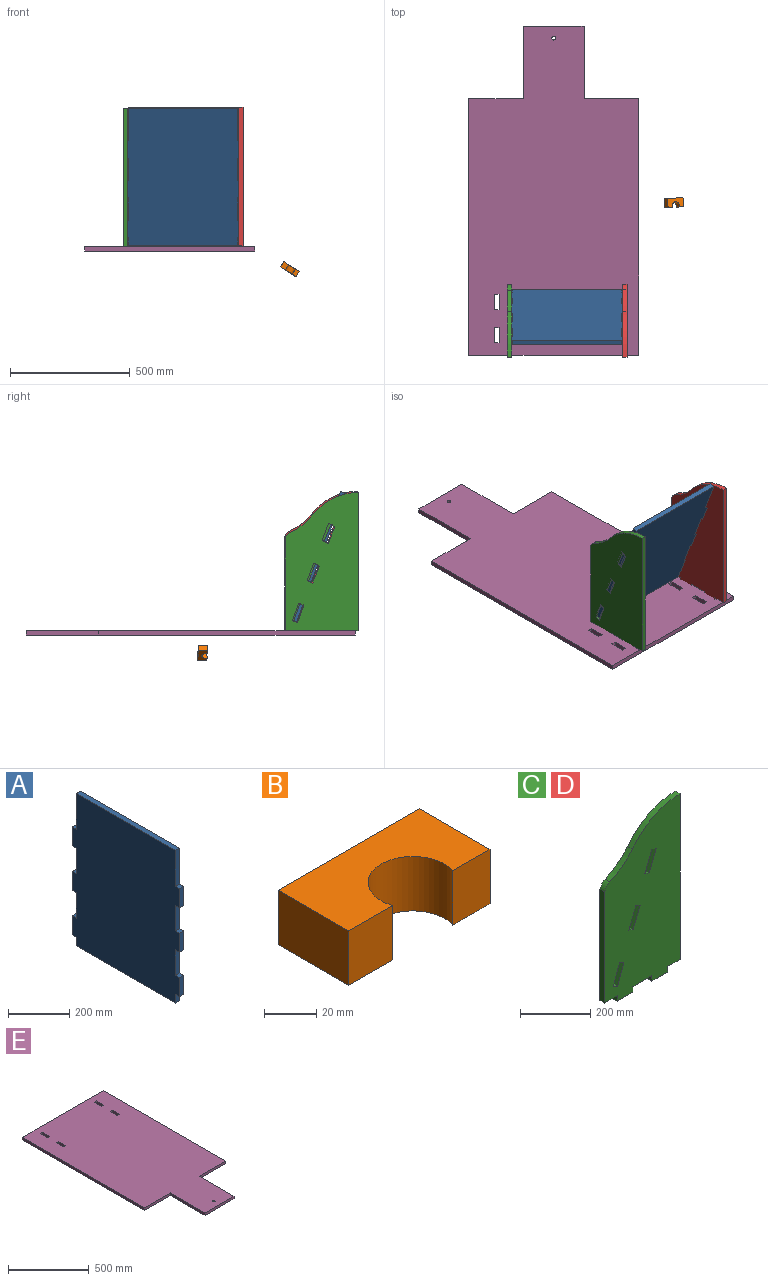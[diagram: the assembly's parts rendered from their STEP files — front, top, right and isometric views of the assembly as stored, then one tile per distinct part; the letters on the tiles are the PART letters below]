
ASSEMBLY  parts=5 mates=1
PART A: 30 faces, bbox 19.1x495.3x609.6 mm
  f0: plane 19.05x19.05mm, normal (0,0,-1), area 362.9mm2, adj f1,f27,f28,f29
  f1: plane 34.46x19.05mm, normal (0,-1,0), area 656.5mm2, adj f0,f2,f28,f29
  f2: plane 457.2x19.05mm, normal (0,0,-1), area 8709.7mm2, adj f1,f3,f28,f29
  f3: plane 34.46x19.05mm, normal (0,1,0), area 656.5mm2, adj f2,f4,f28,f29
  f4: plane 19.05x19.05mm, normal (0,0,-1), area 362.9mm2, adj f3,f5,f28,f29
  f5: plane 76.2x19.05mm, normal (0,1,0), area 1451.6mm2, adj f4,f6,f28,f29
  f6: plane 19.05x19.05mm, normal (0,0,1), area 362.9mm2, adj f5,f7,f28,f29
  f7: plane 101.6x19.05mm, normal (0,1,0), area 1935.5mm2, adj f6,f8,f28,f29
  f8: plane 19.05x19.05mm, normal (0,0,-1), area 362.9mm2, adj f7,f9,f28,f29
  f9: plane 76.2x19.05mm, normal (0,1,0), area 1451.6mm2, adj f8,f10,f28,f29
  f10: plane 19.05x19.05mm, normal (0,0,1), area 362.9mm2, adj f9,f11,f28,f29
  f11: plane 101.6x19.05mm, normal (0,1,0), area 1935.5mm2, adj f10,f12,f28,f29
  f12: plane 19.05x19.05mm, normal (0,0,-1), area 362.9mm2, adj f11,f13,f28,f29
  f13: plane 76.2x19.05mm, normal (0,1,0), area 1451.6mm2, adj f12,f14,f28,f29
  f14: plane 19.05x19.05mm, normal (0,0,1), area 362.9mm2, adj f13,f15,f28,f29
  f15: plane 143.34x19.05mm, normal (0,1,0), area 2730.6mm2, adj f14,f16,f28,f29
  f16: plane 457.2x19.05mm, normal (0,0,1), area 8709.7mm2, adj f15,f17,f28,f29
  f17: plane 143.34x19.05mm, normal (0,-1,0), area 2730.6mm2, adj f16,f18,f28,f29
  f18: plane 19.05x19.05mm, normal (0,0,1), area 362.9mm2, adj f17,f19,f28,f29
  f19: plane 76.2x19.05mm, normal (0,-1,0), area 1451.6mm2, adj f18,f20,f28,f29
  f20: plane 19.05x19.05mm, normal (0,0,-1), area 362.9mm2, adj f19,f21,f28,f29
  f21: plane 101.6x19.05mm, normal (0,-1,0), area 1935.5mm2, adj f20,f22,f28,f29
  f22: plane 19.05x19.05mm, normal (0,0,1), area 362.9mm2, adj f21,f23,f28,f29
  f23: plane 76.2x19.05mm, normal (0,-1,0), area 1451.6mm2, adj f22,f24,f28,f29
  f24: plane 19.05x19.05mm, normal (0,0,-1), area 362.9mm2, adj f23,f25,f28,f29
  f25: plane 101.6x19.05mm, normal (0,-1,0), area 1935.5mm2, adj f24,f26,f28,f29
  f26: plane 19.05x19.05mm, normal (0,0,1), area 362.9mm2, adj f25,f27,f28,f29
  f27: plane 76.2x19.05mm, normal (0,-1,0), area 1451.6mm2, adj f0,f26,f28,f29
  f28: plane 609.6x495.3mm, normal (1,0,0), area 287418.8mm2, adj f0,f1,f2,f3,f4,f5,f6,f7
  f29: plane 609.6x495.3mm, normal (-1,0,0), area 287418.8mm2, adj f0,f1,f2,f3,f4,f5,f6,f7
PART B: 8 faces, bbox 76.2x38.1x25.4 mm
  f0: plane 25.4x23.76mm, normal (0,-1,0), area 603.6mm2, adj f1,f2,f3,f7
  f1: plane 76.2x38.1mm, normal (0,0,1), area 2262.4mm2, adj f0,f3,f4,f5,f6,f7
  f2: plane 76.2x38.1mm, normal (0,0,-1), area 2262.4mm2, adj f0,f3,f4,f5,f6,f7
  f3: plane 38.1x25.4mm, normal (-1,0,0), area 967.7mm2, adj f0,f1,f2,f6
  f4: plane 25.4x19.95mm, normal (0,-1,0), area 506.8mm2, adj f1,f2,f5,f7
  f5: plane 38.1x25.4mm, normal (1,0,0), area 967.7mm2, adj f1,f2,f4,f6
  f6: plane 76.2x25.4mm, normal (0,1,0), area 1935.5mm2, adj f1,f2,f3,f5
  f7: cylinder r=17.11mm len=34.22mm, axis (0,0,-1), area 1643.2mm2, adj f0,f1,f2,f4
PART C: 28 faces, bbox 304.8x19.1x596.5 mm
  f0: plane 70.92x27.87mm, normal (0.93,0,-0.37), area 1451.6mm2, adj f1,f25,f26,f27
  f1: plane 19.05x17.73mm, normal (-0.37,0,-0.93), area 362.9mm2, adj f0,f2,f26,f27
  f2: plane 70.92x27.87mm, normal (-0.93,0,0.37), area 1451.6mm2, adj f1,f25,f26,f27
  f3: plane 577.48x19.05mm, normal (1,0,0), area 11001.1mm2, adj f4,f22,f26,f27
  f4: cylinder r=239.96mm len=192.98mm, axis (0,1,0), area 4271.1mm2, adj f3,f5,f26,f27
  f5: cylinder r=257.98mm len=90.2mm, axis (0,1,0), area 2179.2mm2, adj f4,f6,f26,f27
  f6: cylinder r=43.94mm len=23.45mm, axis (0,1,0), area 621.7mm2, adj f5,f7,f26,f27
  f7: plane 387.88x19.05mm, normal (-1,0,0), area 7389.2mm2, adj f6,f8,f26,f27
  f8: plane 50.8x19.05mm, normal (0,0,-1), area 967.7mm2, adj f7,f9,f26,f27
  f9: plane 19.05x19.05mm, normal (-1,0,0), area 362.9mm2, adj f8,f10,f26,f27
  f10: plane 63.5x19.05mm, normal (0,0,-1), area 1209.7mm2, adj f9,f11,f26,f27
  f11: plane 19.05x19.05mm, normal (1,0,0), area 362.9mm2, adj f10,f12,f26,f27
  f12: plane 76.2x19.05mm, normal (0,0,-1), area 1451.6mm2, adj f11,f13,f26,f27
  f13: plane 19.05x19.05mm, normal (-1,0,0), area 362.9mm2, adj f12,f14,f26,f27
  f14: plane 63.5x19.05mm, normal (0,0,-1), area 1209.7mm2, adj f13,f15,f26,f27
  f15: plane 19.05x19.05mm, normal (1,0,0), area 362.9mm2, adj f14,f22,f26,f27
  f16: plane 19.05x17.74mm, normal (-0.37,0,-0.93), area 363mm2, adj f17,f23,f26,f27
  f17: plane 71.15x25.9mm, normal (-0.94,0,0.34), area 1442.4mm2, adj f16,f18,f26,f27
  f18: plane 19.05x17.9mm, normal (0.34,0,0.94), area 362.9mm2, adj f17,f23,f26,f27
  f19: plane 19.05x17.73mm, normal (-0.37,0,-0.93), area 362.9mm2, adj f20,f24,f26,f27
  f20: plane 70.92x27.87mm, normal (-0.93,0,0.37), area 1451.6mm2, adj f19,f21,f26,f27
  f21: plane 19.05x17.73mm, normal (0.37,0,0.93), area 362.9mm2, adj f20,f24,f26,f27
  f22: plane 50.8x19.05mm, normal (0,0,-1), area 967.7mm2, adj f3,f15,f26,f27
  f23: plane 71.6x26.06mm, normal (0.94,0,-0.34), area 1451.6mm2, adj f16,f18,f26,f27
  f24: plane 70.92x27.87mm, normal (0.93,0,-0.37), area 1451.6mm2, adj f19,f21,f26,f27
  f25: plane 19.05x17.73mm, normal (0.37,0,0.93), area 362.9mm2, adj f0,f2,f26,f27
  f26: plane 596.53x304.8mm, normal (0,-1,0), area 152296.2mm2, adj f0,f1,f2,f3,f4,f5,f6,f7
  f27: plane 596.53x304.8mm, normal (0,1,0), area 152296.2mm2, adj f0,f1,f2,f3,f4,f5,f6,f7
PART D: same geometry as C
PART E: 27 faces, bbox 711.2x1376.8x19.1 mm
  f0: plane 63.5x19.05mm, normal (1,0,0), area 1209.7mm2, adj f1,f23,f24,f25
  f1: plane 19.05x19.05mm, normal (0,-1,0), area 362.9mm2, adj f0,f2,f24,f25
  f2: plane 63.5x19.05mm, normal (-1,0,0), area 1209.7mm2, adj f1,f23,f24,f25
  f3: plane 63.5x19.05mm, normal (-1,0,0), area 1209.7mm2, adj f4,f19,f24,f25
  f4: plane 19.05x19.05mm, normal (0,1,0), area 362.9mm2, adj f3,f5,f24,f25
  f5: plane 63.5x19.05mm, normal (1,0,0), area 1209.7mm2, adj f4,f19,f24,f25
  f6: plane 19.05x19.05mm, normal (0,-1,0), area 362.9mm2, adj f7,f20,f24,f25
  f7: plane 63.5x19.05mm, normal (-1,0,0), area 1209.7mm2, adj f6,f8,f24,f25
  f8: plane 19.05x19.05mm, normal (0,1,0), area 362.9mm2, adj f7,f20,f24,f25
  f9: plane 19.05x19.05mm, normal (0,-1,0), area 362.9mm2, adj f10,f21,f24,f25
  f10: plane 63.5x19.05mm, normal (-1,0,0), area 1209.7mm2, adj f9,f11,f24,f25
  f11: plane 19.05x19.05mm, normal (0,1,0), area 362.9mm2, adj f10,f21,f24,f25
  f12: plane 254x19.05mm, normal (0,-1,0), area 4838.7mm2, adj f13,f22,f24,f25
  f13: plane 304.8x19.05mm, normal (1,0,0), area 5806.4mm2, adj f12,f14,f24,f25
  f14: plane 228.6x19.05mm, normal (0,-1,0), area 4354.8mm2, adj f13,f15,f24,f25
  f15: plane 1072.05x19.05mm, normal (1,0,0), area 20422.5mm2, adj f14,f16,f24,f25
  f16: plane 711.2x19.05mm, normal (0,1,0), area 13548.4mm2, adj f15,f17,f24,f25
  f17: plane 1072.05x19.05mm, normal (-1,0,0), area 20422.5mm2, adj f16,f18,f24,f25
  f18: plane 228.6x19.05mm, normal (0,-1,0), area 4354.8mm2, adj f17,f22,f24,f25
  f19: plane 19.05x19.05mm, normal (0,-1,0), area 362.9mm2, adj f3,f5,f24,f25
  f20: plane 63.5x19.05mm, normal (1,0,0), area 1209.7mm2, adj f6,f8,f24,f25
  f21: plane 63.5x19.05mm, normal (1,0,0), area 1209.7mm2, adj f9,f11,f24,f25
  f22: plane 304.8x19.05mm, normal (-1,0,0), area 5806.4mm2, adj f12,f18,f24,f25
  f23: plane 19.05x19.05mm, normal (0,1,0), area 362.9mm2, adj f0,f2,f24,f25
  f24: plane 1376.85x711.2mm, normal (0,0,1), area 834824mm2, adj f0,f1,f2,f3,f4,f5,f6,f7
  f25: plane 1376.85x711.2mm, normal (0,0,-1), area 834824mm2, adj f0,f1,f2,f3,f4,f5,f6,f7
  f26: cylinder r=7.94mm len=19.05mm, axis (0,0,1), area 950.1mm2, adj f24,f25
PLACE A rot(axis=(0.17,0.17,-0.97),91.8deg) t=(-301.22,-364.46,33.15)mm
PLACE B rot(axis=(-0.01,1,0.06),33deg) t=(371.81,-19.99,-86.35)mm
PLACE C rot(axis=(0,0,-1),90deg) t=(-304.76,-484.05,353.32)mm
PLACE D rot(axis=(0,0,-1),90deg) t=(178.62,-481.38,358.45)mm
PLACE E rot(axis=(1,0,0),180deg) t=(-535.15,732.73,21.68)mm
MATE fastened D.f27 <-> D.f27  axis (1,0,0) through (178.62,-537.82,426.13)mm
